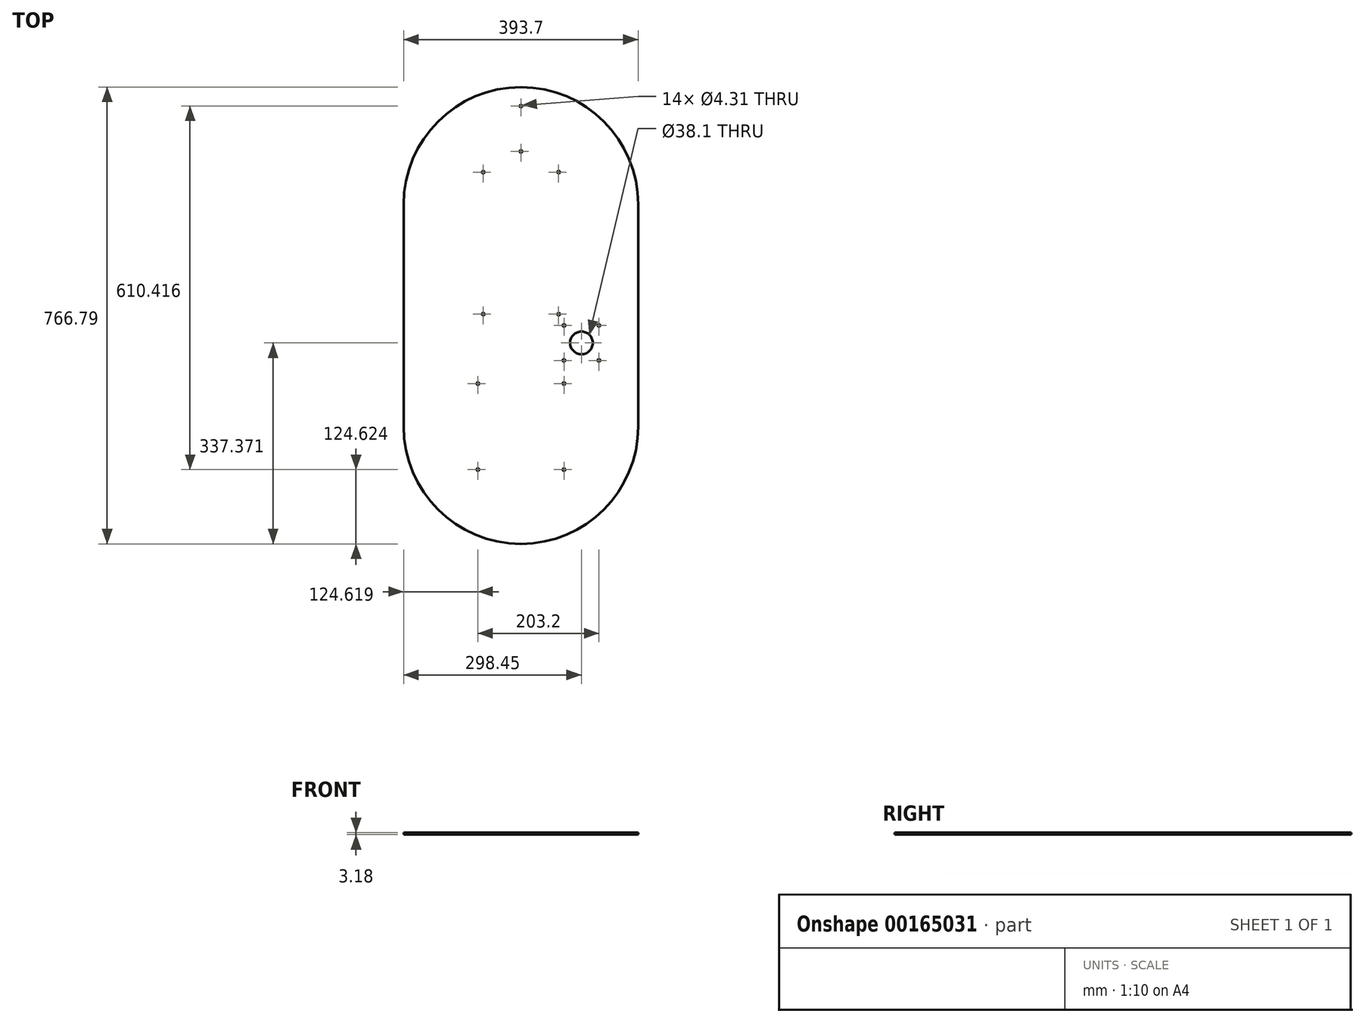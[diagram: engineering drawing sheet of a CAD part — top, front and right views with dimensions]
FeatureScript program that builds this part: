
annotation { "Feature Type Name" : "Feature", "Feature Type Description" : "" }
export const myFeature = defineFeature(function(context is Context, id is Id, definition is map)
    precondition{}
    {
        {
            var Q0;
            Q0=qCreatedBy(makeId("Top.planeOp"),FACE);
            var sketch = newSketch(context, id + "F0", { "sketchPlane" : qUnion([Q0])});
            skLineSegment(sketch, "E0.top", {"start": v(0, -373.09) * mm, "end": v(393.7, -373.09) * mm, "construction": true});
            skLineSegment(sketch, "E0.left", {"start": v(0, 0) * mm, "end": v(0, -373.09) * mm});
            skLineSegment(sketch, "E0.right", {"start": v(393.7, 0) * mm, "end": v(393.7, -373.09) * mm});
            skArc(sketch, "E1", {"start": v(0, -373.09) * mm, "mid": v(196.85, -569.94) * mm, "end": v(393.7, -373.09) * mm});
            skLineSegment(sketch, "E2", {"start": v(196.85, -65.09) * mm, "end": v(196.85, -184.26) * mm, "construction": true});
            skLineSegment(sketch, "E3", {"start": v(196.85, -65.09) * mm, "end": v(196.85, 54.08) * mm, "construction": true});
            skLineSegment(sketch, "E4", {"start": v(133.55, 54.08) * mm, "end": v(260.15, 54.08) * mm, "construction": true});
            skLineSegment(sketch, "E5", {"start": v(260.15, 54.08) * mm, "end": v(196.85, -65.09) * mm, "construction": true});
            skLineSegment(sketch, "E6", {"start": v(196.85, -65.09) * mm, "end": v(133.55, 54.08) * mm, "construction": true});
            skLineSegment(sketch, "E7", {"start": v(133.55, -184.26) * mm, "end": v(260.15, -184.26) * mm, "construction": true});
            skLineSegment(sketch, "E8", {"start": v(196.85, -184.26) * mm, "end": v(196.85, -232.57) * mm, "construction": true});
            skLineSegment(sketch, "E9", {"start": v(196.85, -232.57) * mm, "end": v(298.45, -232.57) * mm, "construction": true});
            skLineSegment(sketch, "E10.bottom", {"start": v(327.82, -203.2) * mm, "end": v(269.08, -203.2) * mm, "construction": true});
            skLineSegment(sketch, "E10.top", {"start": v(327.82, -261.94) * mm, "end": v(269.08, -261.94) * mm, "construction": true});
            skLineSegment(sketch, "E10.left", {"start": v(327.82, -203.2) * mm, "end": v(327.82, -261.94) * mm, "construction": true});
            skLineSegment(sketch, "E10.right", {"start": v(269.08, -203.2) * mm, "end": v(269.08, -261.94) * mm, "construction": true});
            skPoint(sketch, "E10.middle", {"position": v(298.45, -232.57) * mm});
            skLineSegment(sketch, "E11.bottom", {"start": v(269.08, -300.85) * mm, "end": v(124.62, -300.85) * mm, "construction": true});
            skLineSegment(sketch, "E11.top", {"start": v(269.08, -445.32) * mm, "end": v(124.62, -445.32) * mm, "construction": true});
            skLineSegment(sketch, "E11.left", {"start": v(269.08, -300.85) * mm, "end": v(269.08, -445.32) * mm, "construction": true});
            skLineSegment(sketch, "E11.right", {"start": v(124.62, -300.85) * mm, "end": v(124.62, -445.32) * mm, "construction": true});
            skCircle(sketch, "E12", {"center": v(124.62, -300.85) * mm, "radius": 2.15 * mm});
            skCircle(sketch, "E13", {"center": v(269.08, -300.85) * mm, "radius": 2.15 * mm});
            skCircle(sketch, "E14", {"center": v(124.62, -445.32) * mm, "radius": 2.15 * mm});
            skCircle(sketch, "E15", {"center": v(269.08, -445.32) * mm, "radius": 2.15 * mm});
            skCircle(sketch, "E16", {"center": v(269.08, -203.2) * mm, "radius": 2.15 * mm});
            skCircle(sketch, "E17", {"center": v(269.08, -261.94) * mm, "radius": 2.15 * mm});
            skCircle(sketch, "E18", {"center": v(327.82, -261.94) * mm, "radius": 2.15 * mm});
            skCircle(sketch, "E19", {"center": v(327.82, -203.2) * mm, "radius": 2.15 * mm});
            skCircle(sketch, "E20", {"center": v(133.55, -184.26) * mm, "radius": 2.15 * mm});
            skCircle(sketch, "E21", {"center": v(260.15, -184.26) * mm, "radius": 2.15 * mm});
            skCircle(sketch, "E22", {"center": v(260.15, 54.08) * mm, "radius": 2.15 * mm});
            skCircle(sketch, "E23", {"center": v(133.55, 54.08) * mm, "radius": 2.15 * mm});
            skLineSegment(sketch, "E24", {"start": v(0, 0) * mm, "end": v(131.23, 0) * mm, "construction": true});
            skLineSegment(sketch, "E25", {"start": v(131.23, 0) * mm, "end": v(131.23, -65.09) * mm, "construction": true});
            skLineSegment(sketch, "E26", {"start": v(131.23, -65.09) * mm, "end": v(262.47, -65.09) * mm, "construction": true});
            skLineSegment(sketch, "E27", {"start": v(262.47, -65.09) * mm, "end": v(262.47, 0) * mm, "construction": true});
            skLineSegment(sketch, "E28", {"start": v(262.47, 0) * mm, "end": v(393.7, 0) * mm, "construction": true});
            skArc(sketch, "E29", {"start": v(393.7, 0) * mm, "mid": v(196.85, 196.85) * mm, "end": v(0, 0) * mm});
            skLineSegment(sketch, "E30", {"start": v(196.85, 196.85) * mm, "end": v(196.85, 165.1) * mm, "construction": true});
            skLineSegment(sketch, "E31", {"start": v(196.85, 165.1) * mm, "end": v(196.85, 88.9) * mm, "construction": true});
            skCircle(sketch, "E32", {"center": v(196.85, 165.1) * mm, "radius": 2.15 * mm});
            skCircle(sketch, "E33", {"center": v(196.85, 88.9) * mm, "radius": 2.15 * mm});
            skCircle(sketch, "E34", {"center": v(298.45, -232.57) * mm, "radius": 19.05 * mm});
            skArc(sketch, "E35", {"start": v(260.15, 54.08) * mm, "mid": v(196.85, 69.85) * mm, "end": v(133.55, 54.08) * mm, "construction": true});
            skLineSegment(sketch, "E36", {"start": v(196.85, 88.9) * mm, "end": v(196.85, 69.85) * mm, "construction": true});
            skCircle(sketch, "E37", {"center": v(196.85, -373.09) * mm, "radius": 127 * mm, "construction": true});
            skCircle(sketch, "E38", {"center": v(269.08, -261.94) * mm, "radius": 5.56 * mm, "construction": true});
            skSolve(sketch);
        }
        {
            var Q0;
            Q0=qSketchRegion(id+"F0",true);
            extrude(context, id + "F1", {"entities" : qUnion([Q0]), "depth" : 3.17 * mm});
        }
    });
